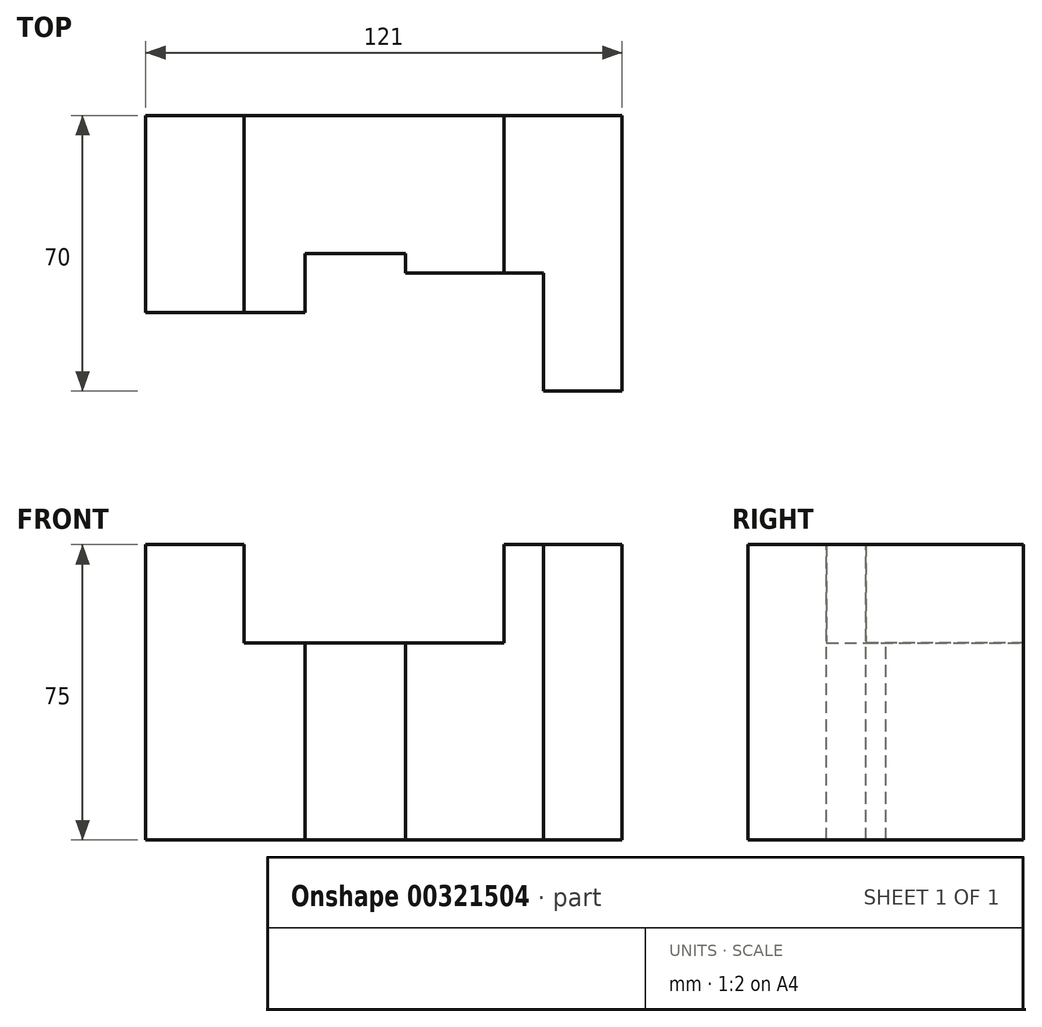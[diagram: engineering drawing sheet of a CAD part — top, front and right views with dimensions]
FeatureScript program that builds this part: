
annotation { "Feature Type Name" : "Feature", "Feature Type Description" : "" }
export const myFeature = defineFeature(function(context is Context, id is Id, definition is map)
    precondition{}
    {
        {
            var Q0;
            Q0=qCreatedBy(makeId("Front.planeOp"),FACE);
            var sketch = newSketch(context, id + "F0", { "sketchPlane" : qUnion([Q0])});
            skLineSegment(sketch, "E0.bottom", {"start": v(0, 0) * mm, "end": v(40.5, 0) * mm});
            skLineSegment(sketch, "E0.top", {"start": v(0, 75) * mm, "end": v(25, 75) * mm});
            skLineSegment(sketch, "E0.left", {"start": v(0, 0) * mm, "end": v(0, 75) * mm});
            skLineSegment(sketch, "E0.right", {"start": v(40.5, 0) * mm, "end": v(40.5, 50) * mm});
            skPoint(sketch, "E1", {"position": v(25, 75) * mm});
            skPoint(sketch, "E2", {"position": v(25, 50) * mm});
            skLineSegment(sketch, "E3", {"start": v(25, 75) * mm, "end": v(25, 50) * mm});
            skLineSegment(sketch, "E4", {"start": v(25, 50) * mm, "end": v(40.5, 50) * mm});
            skSolve(sketch);
        }
        {
            var Q0;
            Q0 = qSketchRegion(id + "F0", true);
            extrude(context, id + "F1", {"entities" : qUnion([Q0]), "depth" : 50 * mm});
        }
        {
            var Q0;
            Q0=makeQuery(id+"F1.opExtrude","SWEPT_FACE",FACE,{"disambiguationData":[OSD([sQuery(id+"F0.wireOp",EDGE,"E0.right")])]});
            var sketch = newSketch(context, id + "F2", { "sketchPlane" : qUnion([Q0])});
            skLineSegment(sketch, "E5.bottom", {"start": v(0, 0) * mm, "end": v(-35, 0) * mm});
            skLineSegment(sketch, "E5.top", {"start": v(0, 50) * mm, "end": v(-35, 50) * mm});
            skLineSegment(sketch, "E5.left", {"start": v(0, 0) * mm, "end": v(0, 50) * mm});
            skLineSegment(sketch, "E5.right", {"start": v(-35, 0) * mm, "end": v(-35, 50) * mm});
            skSolve(sketch);
        }
        {
            var Q0;
            Q0 = qSketchRegion(id + "F2", true);
            extrude(context, id + "F3", {"entities" : qUnion([Q0]), "operationType" : NewBodyOperationType.ADD, "depth" : 25.5 * mm});
        }
        {
            var Q0;
            Q0=makeQuery(id+"F3.opExtrude","CAP_FACE",FACE,{"disambiguationData":[OSD([sQuery(id+"F2.wireOp",EDGE,"E5.bottom"),sQuery(id+"F2.wireOp",EDGE,"E5.top"),sQuery(id+"F2.wireOp",EDGE,"E5.left"),sQuery(id+"F2.wireOp",EDGE,"E5.right")])],"isStart":false});
            var sketch = newSketch(context, id + "F4", { "sketchPlane" : qUnion([Q0])});
            skLineSegment(sketch, "E6.bottom", {"start": v(0, 0) * mm, "end": v(-40, 0) * mm});
            skLineSegment(sketch, "E6.top", {"start": v(0, 50) * mm, "end": v(-40, 50) * mm});
            skLineSegment(sketch, "E6.left", {"start": v(0, 0) * mm, "end": v(0, 50) * mm});
            skLineSegment(sketch, "E6.right", {"start": v(-40, 0) * mm, "end": v(-40, 50) * mm});
            skSolve(sketch);
        }
        {
            var Q0;
            Q0 = qSketchRegion(id + "F4", true);
            extrude(context, id + "F5", {"entities" : qUnion([Q0]), "operationType" : NewBodyOperationType.ADD, "depth" : 35 * mm});
        }
        {
            var Q0;
            Q0=makeQuery(id+"F5.boolean.opBoolean","MERGE",FACE,{"derivedFrom":[makeQuery(id+"F3.boolean.opBoolean","MERGE",FACE,{"derivedFrom":[makeQuery(id+"F1.opExtrude","SWEPT_FACE",FACE,{"disambiguationData":[OSD([sQuery(id+"F0.wireOp",EDGE,"E4")])]}),makeQuery(id+"F3.opExtrude","SWEPT_FACE",FACE,{"disambiguationData":[OSD([sQuery(id+"F2.wireOp",EDGE,"E5.top")])]})]}),makeQuery(id+"F5.opExtrude","SWEPT_FACE",FACE,{"disambiguationData":[OSD([sQuery(id+"F4.wireOp",EDGE,"E6.top")])]})]});
            var sketch = newSketch(context, id + "F6", { "sketchPlane" : qUnion([Q0])});
            skLineSegment(sketch, "E7.bottom", {"start": v(101, 0) * mm, "end": v(91, 0) * mm});
            skLineSegment(sketch, "E7.top", {"start": v(101, -40) * mm, "end": v(91, -40) * mm});
            skLineSegment(sketch, "E7.left", {"start": v(101, 0) * mm, "end": v(101, -40) * mm});
            skLineSegment(sketch, "E7.right", {"start": v(91, 0) * mm, "end": v(91, -40) * mm});
            skSolve(sketch);
        }
        {
            var Q0;
            Q0 = qSketchRegion(id + "F6", true);
            extrude(context, id + "F7", {"entities" : qUnion([Q0]), "operationType" : NewBodyOperationType.ADD, "depth" : 25 * mm});
        }
        {
            var Q0;
            Q0=makeQuery(id+"F7.boolean.opBoolean","MERGE",FACE,{"derivedFrom":[makeQuery(id+"F5.opExtrude","CAP_FACE",FACE,{"disambiguationData":[OSD([sQuery(id+"F4.wireOp",EDGE,"E6.bottom"),sQuery(id+"F4.wireOp",EDGE,"E6.top"),sQuery(id+"F4.wireOp",EDGE,"E6.left"),sQuery(id+"F4.wireOp",EDGE,"E6.right")])],"isStart":false}),makeQuery(id+"F7.opExtrude","SWEPT_FACE",FACE,{"disambiguationData":[OSD([sQuery(id+"F6.wireOp",EDGE,"E7.left")])]})]});
            var sketch = newSketch(context, id + "F8", { "sketchPlane" : qUnion([Q0])});
            skLineSegment(sketch, "E8.bottom", {"start": v(0, 0) * mm, "end": v(-70, 0) * mm});
            skLineSegment(sketch, "E8.top", {"start": v(0, 75) * mm, "end": v(-70, 75) * mm});
            skLineSegment(sketch, "E8.left", {"start": v(0, 0) * mm, "end": v(0, 75) * mm});
            skLineSegment(sketch, "E8.right", {"start": v(-70, 0) * mm, "end": v(-70, 75) * mm});
            skSolve(sketch);
        }
        {
            var Q0;
            Q0 = qSketchRegion(id + "F8", true);
            extrude(context, id + "F9", {"entities" : qUnion([Q0]), "operationType" : NewBodyOperationType.ADD, "depth" : 20 * mm});
        }
    });
